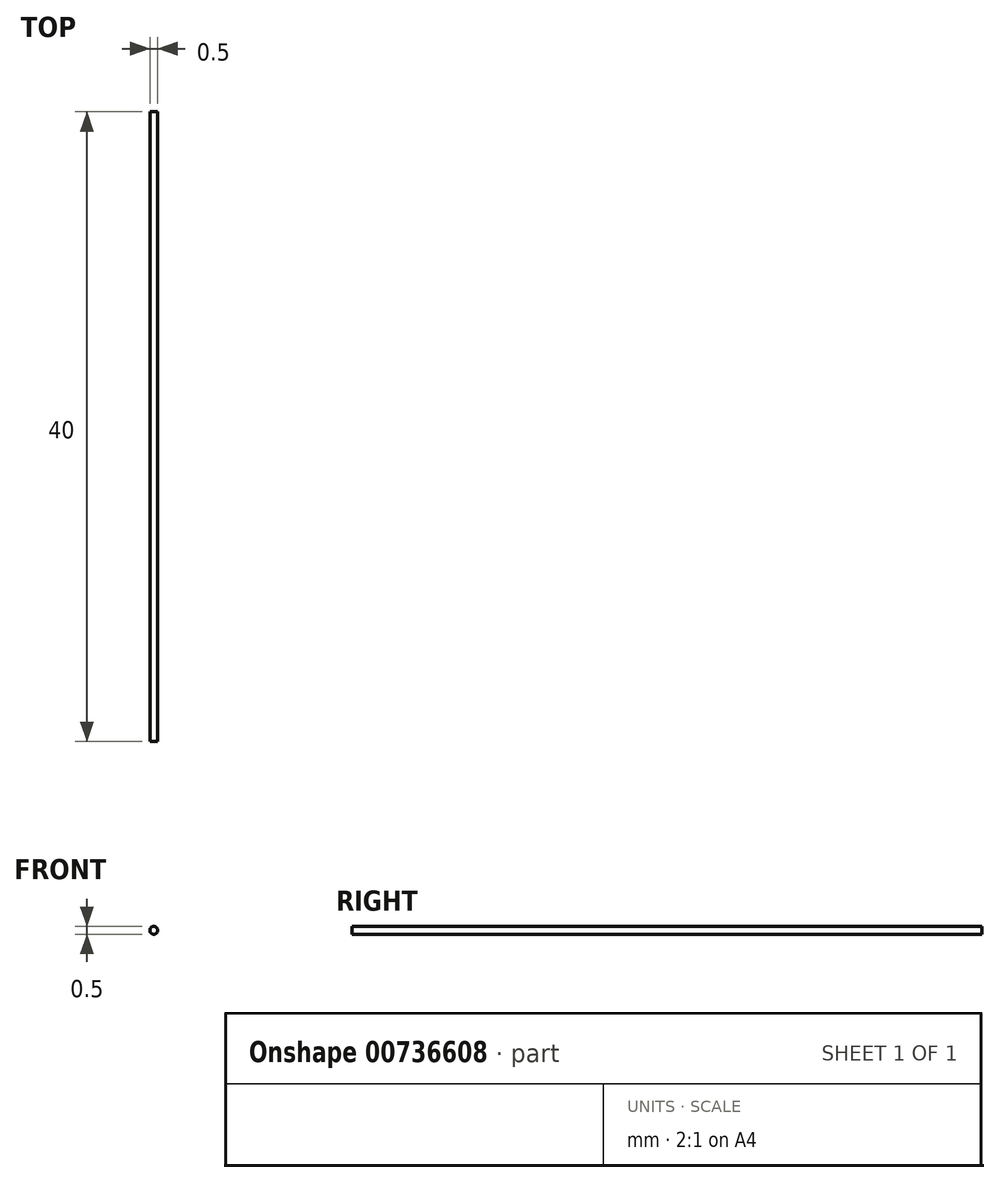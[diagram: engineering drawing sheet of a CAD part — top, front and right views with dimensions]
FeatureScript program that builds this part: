
annotation { "Feature Type Name" : "Feature", "Feature Type Description" : "" }
export const myFeature = defineFeature(function(context is Context, id is Id, definition is map)
    precondition{}
    {
        {
            var Q0;
            Q0=qCreatedBy(makeId("Front.planeOp"),FACE);
            var sketch = newSketch(context, id + "F0", { "sketchPlane" : qUnion([Q0])});
            skCircle(sketch, "E0", {"center": v(0, 0) * mm, "radius": 0.25 * mm});
            skSolve(sketch);
        }
        {
            var Q0;
            Q0 = qSketchRegion(id + "F0", true);
            extrude(context, id + "F1", {"entities" : qUnion([Q0]), "depth" : 40 * mm, "offsetDistance" : 25 * mm, "symmetric" : true});
        }
    });
